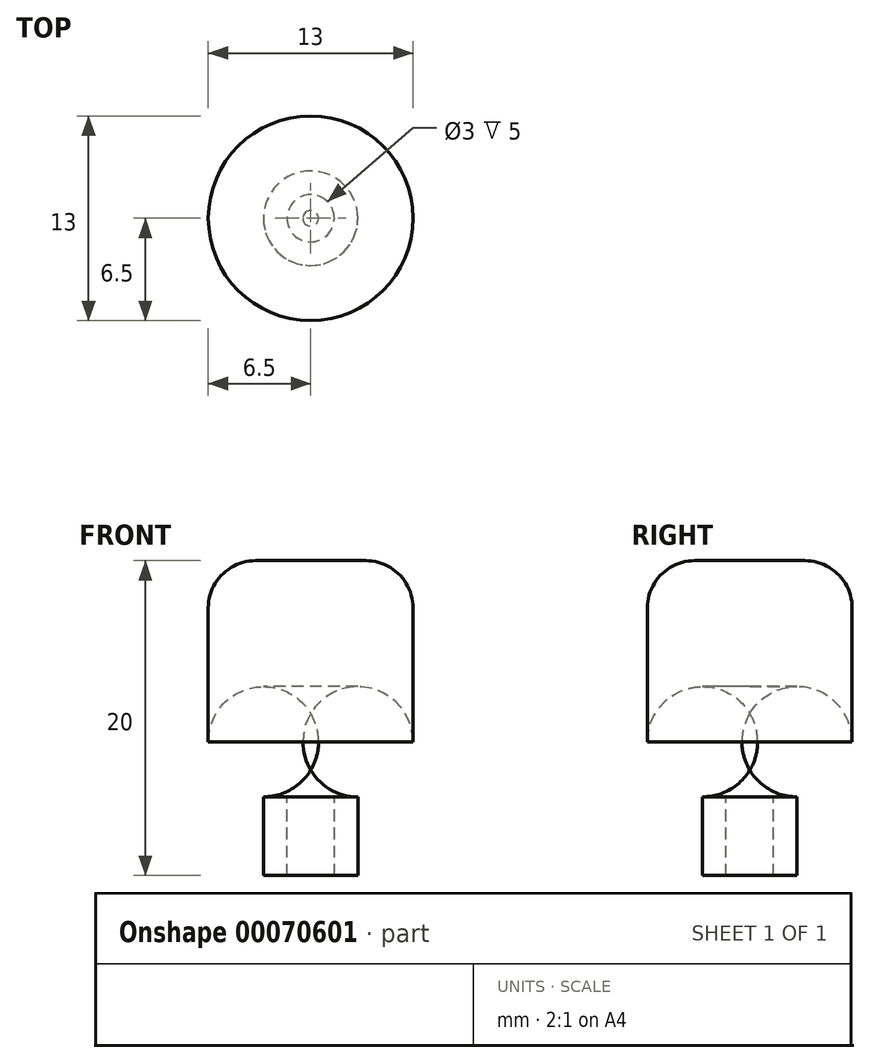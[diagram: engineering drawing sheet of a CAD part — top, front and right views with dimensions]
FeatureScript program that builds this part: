
annotation { "Feature Type Name" : "Feature", "Feature Type Description" : "" }
export const myFeature = defineFeature(function(context is Context, id is Id, definition is map)
    precondition{}
    {
        {
            var Q0;
            Q0=qCreatedBy(makeId("Top.planeOp"),FACE);
            var sketch = newSketch(context, id + "F0", { "sketchPlane" : qUnion([Q0])});
            skCircle(sketch, "E0", {"center": v(0, 0) * mm, "radius": 6.5 * mm});
            skSolve(sketch);
        }
        {
            var Q0;
            Q0=makeQuery(id+"F0.imprint","IMPRINT",FACE,{"disambiguationData":[TD([[makeQuery(id+"F0.imprint","IMPRINT",EDGE,{"derivedFrom":sQuery(id+"F0.wireOp",EDGE,"E0")}),1.0]])]});
            extrude(context, id + "F1", {"entities" : qUnion([Q0]), "depth" : 15 * mm});
        }
        {
            var Q0;
            Q0=makeQuery(id+"F1.opExtrude","CAP_FACE",FACE,{"disambiguationData":[OSD([sQuery(id+"F0.wireOp",EDGE,"E0")])],"isStart":true});
            var sketch = newSketch(context, id + "F2", { "sketchPlane" : qUnion([Q0])});
            skCircle(sketch, "E1", {"center": v(0, 0) * mm, "radius": 1.5 * mm});
            skCircle(sketch, "E2", {"center": v(0, 0) * mm, "radius": 3 * mm});
            skSolve(sketch);
        }
        {
            var Q0;
            Q0=makeQuery(id+"F2.imprint","IMPRINT",FACE,{"disambiguationData":[TD([[makeQuery(id+"F2.imprint","IMPRINT",EDGE,{"derivedFrom":sQuery(id+"F2.wireOp",EDGE,"E1")}),-1.0]])]});
            extrude(context, id + "F3", {"entities" : qUnion([Q0]), "operationType" : NewBodyOperationType.ADD, "depth" : 5 * mm});
        }
        {
            var Q0;
            Q0=makeQuery(id+"F1.opExtrude","CAP_EDGE",EDGE,{"disambiguationData":[OSD([sQuery(id+"F0.wireOp",EDGE,"E0")])],"isStart":true});
            fillet(context, id + "F4", {"entities" : qUnion([Q0]), "radius" : 3.5 * mm, "tangentPropagation" : true, "allowEdgeOverflow" : false});
        }
        {
            var Q0;
            Q0=makeQuery(id+"F1.opExtrude","CAP_EDGE",EDGE,{"disambiguationData":[OSD([sQuery(id+"F0.wireOp",EDGE,"E0")])],"isStart":false});
            fillet(context, id + "F5", {"entities" : qUnion([Q0]), "radius" : 3 * mm, "tangentPropagation" : true, "allowEdgeOverflow" : false});
        }
    });
